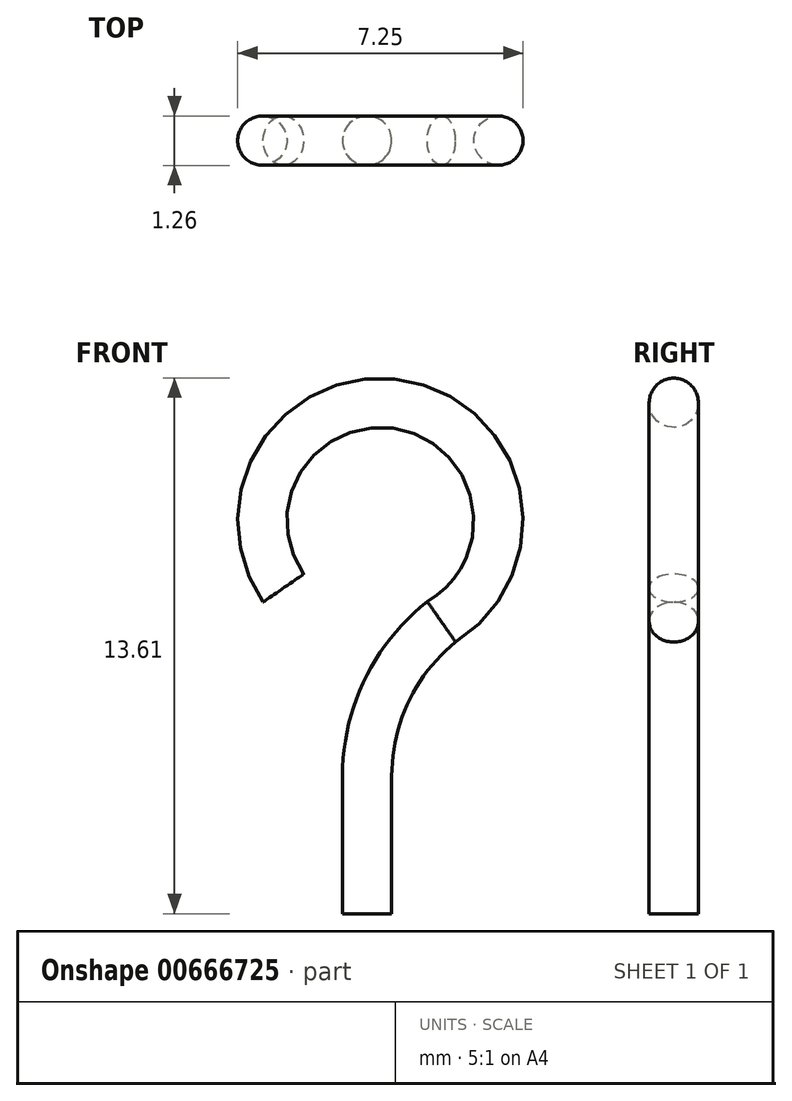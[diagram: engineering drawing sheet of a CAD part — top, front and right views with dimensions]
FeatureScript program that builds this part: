
annotation { "Feature Type Name" : "Feature", "Feature Type Description" : "" }
export const myFeature = defineFeature(function(context is Context, id is Id, definition is map)
    precondition{}
    {
        {
            var Q0;
            Q0=qCreatedBy(makeId("Front.planeOp"),FACE);
            var sketch = newSketch(context, id + "F0", { "sketchPlane" : qUnion([Q0])});
            skLineSegment(sketch, "E0", {"start": v(0, 0) * mm, "end": v(0, 3.5) * mm});
            skArc(sketch, "E1", {"start": v(1.89, 7.41) * mm, "mid": v(0.5, 5.67) * mm, "end": v(0, 3.5) * mm});
            skArc(sketch, "E2", {"start": v(1.89, 7.41) * mm, "mid": v(0.96, 12.92) * mm, "end": v(-2.13, 8.27) * mm});
            skSolve(sketch);
        }
        {
            var Q0;
            Q0=qCreatedBy(makeId("Top.planeOp"),FACE);
            var sketch = newSketch(context, id + "F1", { "sketchPlane" : qUnion([Q0])});
            skCircle(sketch, "E3", {"center": v(0, 0) * mm, "radius": 0.62 * mm});
            skSolve(sketch);
        }
        {
            var Q0;
            Q0 = qSketchRegion(id + "F1", true);
            var Q1;
            Q1=sQuery(id+"F0.wireOp",EDGE,"E0");
            var Q2;
            Q2=sQuery(id+"F0.wireOp",EDGE,"E1");
            var Q3;
            Q3=sQuery(id+"F0.wireOp",EDGE,"E2");
            sweep(context, id + "F2", {"profiles" : qUnion([Q0]), "path" : qUnion([Q1, Q2, Q3])});
        }
    });
